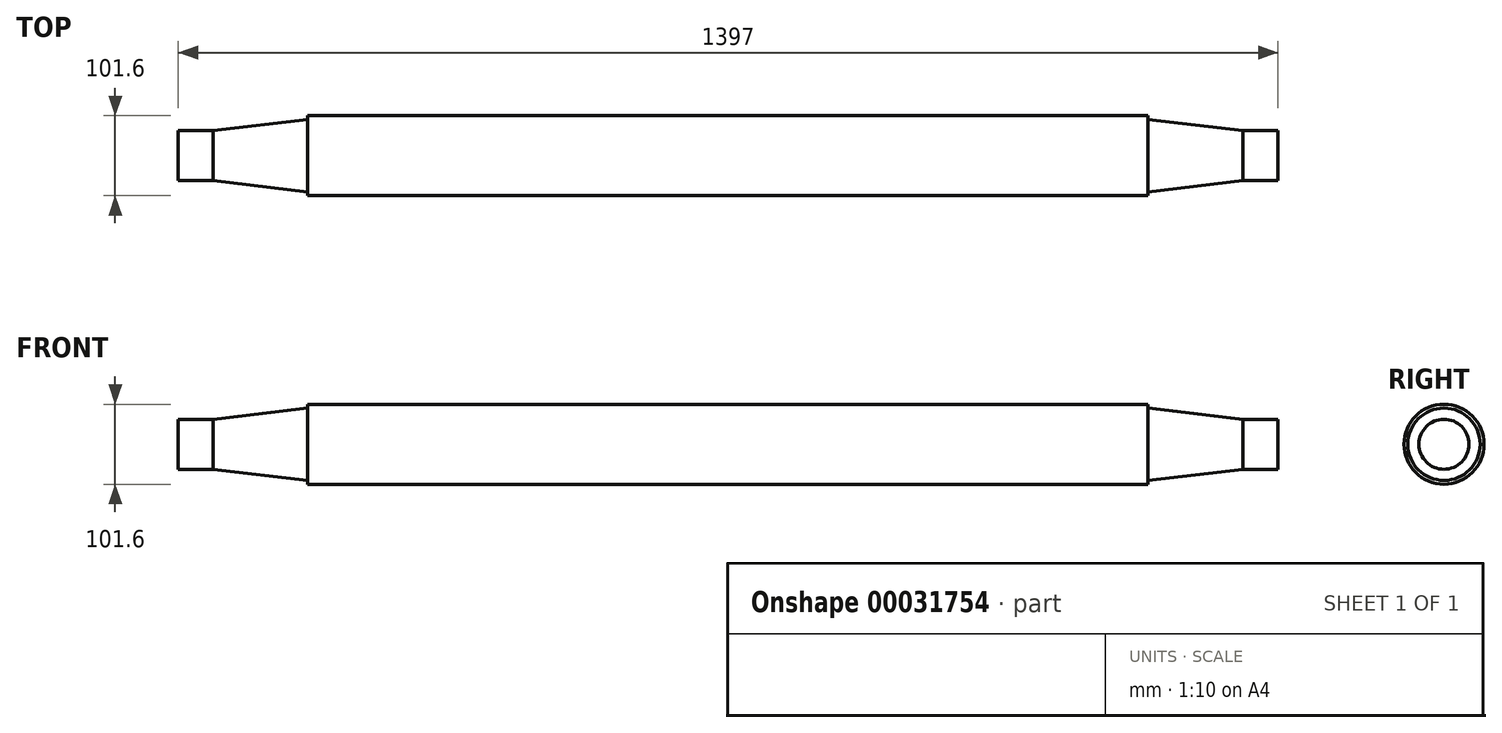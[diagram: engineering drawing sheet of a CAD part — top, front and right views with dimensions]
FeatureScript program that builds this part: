
annotation { "Feature Type Name" : "Feature", "Feature Type Description" : "" }
export const myFeature = defineFeature(function(context is Context, id is Id, definition is map)
    precondition{}
    {
        {
            var Q0;
            Q0=qCreatedBy(makeId("Front.planeOp"),FACE);
            var sketch = newSketch(context, id + "F0", { "sketchPlane" : qUnion([Q0])});
            skLineSegment(sketch, "E0", {"start": v(-698.5, 0) * mm, "end": v(698.5, 0) * mm});
            skLineSegment(sketch, "E1.0", {"start": v(-533.97, 50.8) * mm, "end": v(533.4, 50.8) * mm});
            skLineSegment(sketch, "E2.0", {"start": v(-698.5, 31.75) * mm, "end": v(-654.05, 31.75) * mm});
            skLineSegment(sketch, "E3", {"start": v(-698.5, 31.75) * mm, "end": v(-698.5, 0) * mm});
            skLineSegment(sketch, "E4", {"start": v(-533.4, 45.97) * mm, "end": v(-654.05, 31.75) * mm});
            skLineSegment(sketch, "E5", {"start": v(-533.4, 45.97) * mm, "end": v(-533.97, 50.8) * mm});
            skLineSegment(sketch, "E6", {"start": v(0, 0) * mm, "end": v(0, -221) * mm, "construction": true});
            skLineSegment(sketch, "E7.MirrorCS", {"start": v(698.5, 31.75) * mm, "end": v(698.5, 0) * mm});
            skLineSegment(sketch, "E8.MirrorCS", {"start": v(698.5, 31.75) * mm, "end": v(654.05, 31.75) * mm});
            skLineSegment(sketch, "E9.MirrorCS", {"start": v(533.4, 45.97) * mm, "end": v(654.05, 31.75) * mm});
            skLineSegment(sketch, "E10", {"start": v(533.4, 45.97) * mm, "end": v(533.4, 50.8) * mm});
            skSolve(sketch);
        }
        {
            var Q0;
            Q0 = qSketchRegion(id + "F0", true);
            var Q1;
            Q1=sQuery(id+"F0.wireOp",EDGE,"E0");
            revolve(context, id + "F1", {"entities" : qUnion([Q0]), "axis" : qUnion([Q1]), "revolveType" : RevolveType.FULL});
        }
    });
